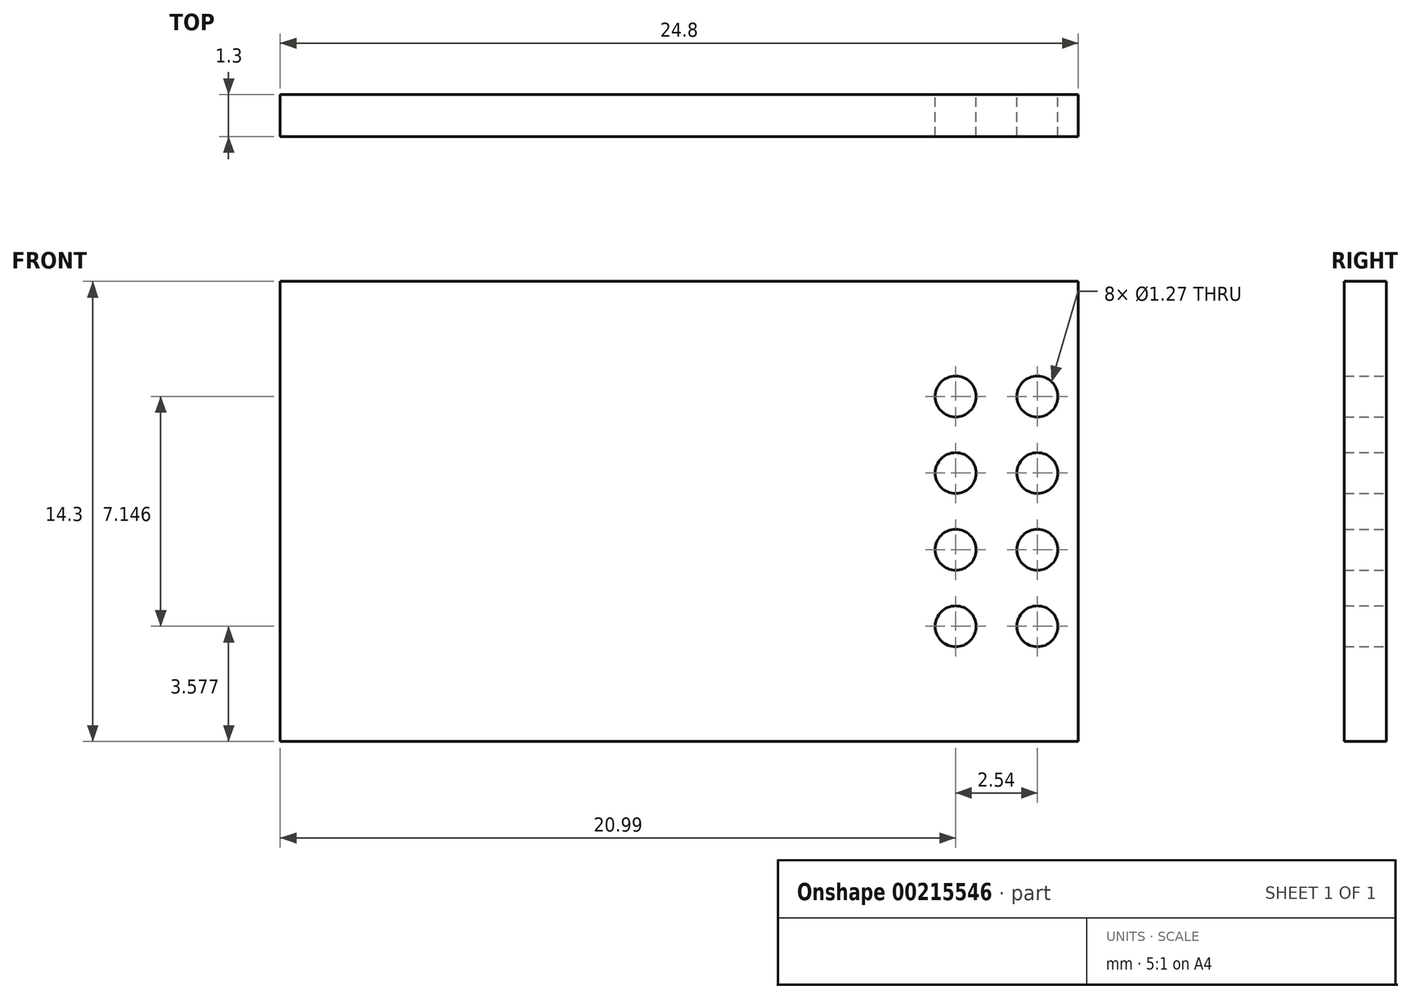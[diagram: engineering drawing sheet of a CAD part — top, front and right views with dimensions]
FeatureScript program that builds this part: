
annotation { "Feature Type Name" : "Feature", "Feature Type Description" : "" }
export const myFeature = defineFeature(function(context is Context, id is Id, definition is map)
    precondition{}
    {
        {
            var Q0;
            Q0=qCreatedBy(makeId("Front.planeOp"),FACE);
            var sketch = newSketch(context, id + "F0", { "sketchPlane" : qUnion([Q0])});
            skLineSegment(sketch, "E0.bottom", {"start": v(0, 0) * mm, "end": v(24.8, 0) * mm});
            skLineSegment(sketch, "E0.top", {"start": v(0, 14.3) * mm, "end": v(24.8, 14.3) * mm});
            skLineSegment(sketch, "E0.left", {"start": v(0, 0) * mm, "end": v(0, 14.3) * mm});
            skLineSegment(sketch, "E0.right", {"start": v(24.8, 0) * mm, "end": v(24.8, 14.3) * mm});
            skCircle(sketch, "E1", {"center": v(23.53, 10.72) * mm, "radius": 0.64 * mm});
            skCircle(sketch, "E2.1.0.0", {"center": v(23.53, 8.34) * mm, "radius": 0.64 * mm});
            skCircle(sketch, "E2.2.0.0", {"center": v(23.53, 5.96) * mm, "radius": 0.64 * mm});
            skLineSegment(sketch, "E2.direction1", {"start": v(23.53, 10.72) * mm, "end": v(23.53, 8.34) * mm, "construction": true});
            skLineSegment(sketch, "E3", {"start": v(23.53, 10.72) * mm, "end": v(23.53, 14.3) * mm, "construction": true});
            skCircle(sketch, "E4.0.3.0", {"center": v(23.53, 3.58) * mm, "radius": 0.64 * mm});
            skLineSegment(sketch, "E5", {"start": v(23.53, 5.96) * mm, "end": v(23.53, 8.34) * mm, "construction": true});
            skLineSegment(sketch, "E6", {"start": v(23.53, 7.15) * mm, "end": v(21.38, 7.15) * mm, "construction": true});
            skLineSegment(sketch, "E7", {"start": v(22.26, 14.3) * mm, "end": v(22.26, 0) * mm, "construction": true});
            skCircle(sketch, "E8.MirrorC", {"center": v(20.99, 10.72) * mm, "radius": 0.64 * mm});
            skCircle(sketch, "E9.MirrorC", {"center": v(21, 8.34) * mm, "radius": 0.64 * mm});
            skCircle(sketch, "E10.MirrorC", {"center": v(21, 5.96) * mm, "radius": 0.64 * mm});
            skCircle(sketch, "E11.MirrorC", {"center": v(20.99, 3.58) * mm, "radius": 0.64 * mm});
            skSolve(sketch);
        }
        {
            var Q0;
            Q0 = qSketchRegion(id + "F0", true);
            extrude(context, id + "F1", {"entities" : qUnion([Q0]), "depth" : 1.3 * mm});
        }
    });
